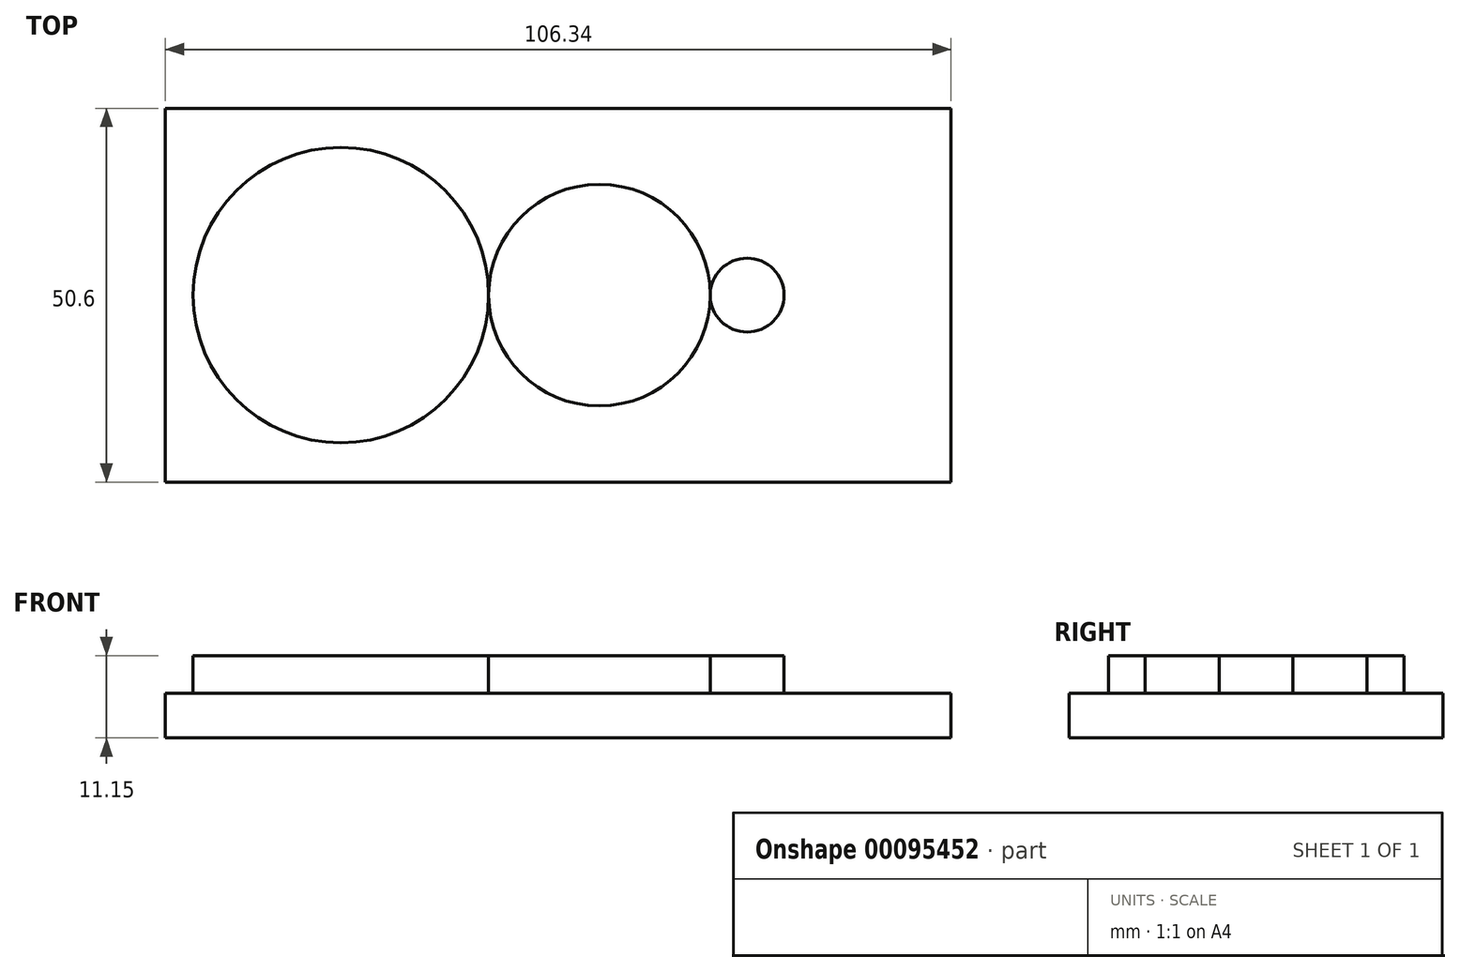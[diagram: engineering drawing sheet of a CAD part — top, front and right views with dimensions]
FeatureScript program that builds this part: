
annotation { "Feature Type Name" : "Feature", "Feature Type Description" : "" }
export const myFeature = defineFeature(function(context is Context, id is Id, definition is map)
    precondition{}
    {
        {
            var Q0;
            Q0=qCreatedBy(makeId("Top.planeOp"),FACE);
            var sketch = newSketch(context, id + "F0", { "sketchPlane" : qUnion([Q0])});
            skLineSegment(sketch, "E0.bottom", {"start": v(-53.17, 25.3) * mm, "end": v(53.17, 25.3) * mm});
            skLineSegment(sketch, "E0.top", {"start": v(-53.17, -25.3) * mm, "end": v(53.17, -25.3) * mm});
            skLineSegment(sketch, "E0.left", {"start": v(-53.17, 25.3) * mm, "end": v(-53.17, -25.3) * mm});
            skLineSegment(sketch, "E0.right", {"start": v(53.17, 25.3) * mm, "end": v(53.17, -25.3) * mm});
            skPoint(sketch, "E0.middle", {"position": v(0, 0) * mm});
            skSolve(sketch);
        }
        {
            var Q0;
            Q0=makeQuery(id+"F0.imprint","IMPRINT",FACE,{"disambiguationData":[TD([[makeQuery(id+"F0.imprint","IMPRINT",EDGE,{"derivedFrom":sQuery(id+"F0.wireOp",EDGE,"E0.bottom")}),-1.0]])]});
            var sketch = newSketch(context, id + "F1", { "sketchPlane" : qUnion([Q0])});
            skCircle(sketch, "E1", {"center": v(-29.43, 0) * mm, "radius": 20 * mm});
            skCircle(sketch, "E2", {"center": v(5.57, 0) * mm, "radius": 15 * mm});
            skCircle(sketch, "E3", {"center": v(25.58, 0) * mm, "radius": 5 * mm});
            skSolve(sketch);
        }
        {
            var Q0;
            Q0=makeQuery(id+"F1.imprint","IMPRINT",FACE,{"disambiguationData":[TD([[makeQuery(id+"F1.imprint","IMPRINT",EDGE,{"derivedFrom":sQuery(id+"F1.wireOp",EDGE,"E3")}),1.0]])]});
            var Q1;
            {var subQ0=sQuery(id+"F1.wireOp",EDGE,"E2");var subQ1=makeQuery(id+"F1.imprint","INTERSECT",VERTEX,{"derivedFrom":[sQuery(id+"F1.wireOp",EDGE,"E1"),subQ0]});Q1=makeQuery(id+"F1.imprint","IMPRINT",FACE,{"disambiguationData":[TD([[makeQuery(id+"F1.imprint","IMPRINT",EDGE,{"disambiguationData":[TD([[subQ1,1.0]])],"derivedFrom":subQ0}),1.0]])]});}
            var Q2;
            Q2=makeQuery(id+"F1.imprint","IMPRINT",FACE,{"disambiguationData":[TD([[makeQuery(id+"F1.imprint","IMPRINT",EDGE,{"derivedFrom":sQuery(id+"F1.wireOp",EDGE,"E1")}),1.0]])]});
            extrude(context, id + "F2", {"entities" : qUnion([Q0, Q1, Q2]), "depth" : 5.08 * mm});
        }
        {
            var Q0;
            Q0=makeQuery(id+"F0.imprint","IMPRINT",FACE,{"disambiguationData":[TD([[makeQuery(id+"F0.imprint","IMPRINT",EDGE,{"derivedFrom":sQuery(id+"F0.wireOp",EDGE,"E0.bottom")}),-1.0]])]});
            extrude(context, id + "F3", {"entities" : qUnion([Q0]), "oppositeDirection" : true, "depth" : 6.07 * mm});
        }
    });
